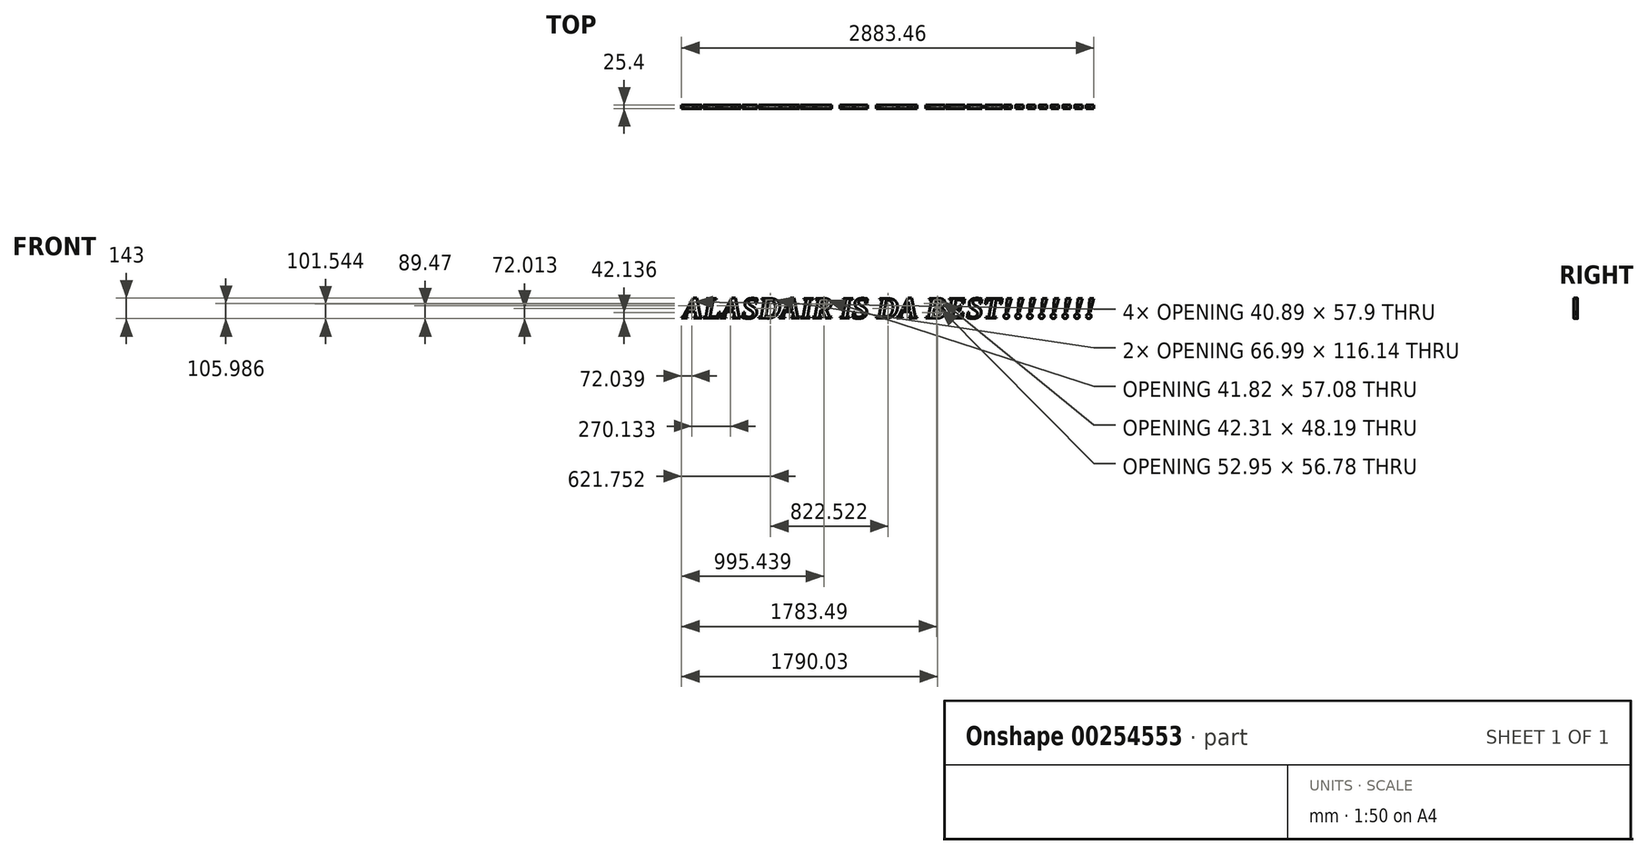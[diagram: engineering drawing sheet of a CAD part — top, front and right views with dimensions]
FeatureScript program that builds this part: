
annotation { "Feature Type Name" : "Feature", "Feature Type Description" : "" }
export const myFeature = defineFeature(function(context is Context, id is Id, definition is map)
    precondition{}
    {
        {
            var Q0;
            Q0=qCreatedBy(makeId("Front.planeOp"),FACE);
            var sketch = newSketch(context, id + "F0", { "sketchPlane" : qUnion([Q0])});
            skText(sketch, "E0", { "text": "ALASDAIR IS DA BEST!!!!!!!!", "fontName": "Tinos-BoldItalic.ttf"});
            const initialGuessF0  = {"E0": [-0.07596, -0.07625, 1, 0, 0.15221]};
            skSetInitialGuess(sketch, initialGuessF0);
            skSolve(sketch);
        }
        {
            var Q0;
            Q0 = qSketchRegion(id + "F0", true);
            var Q1;
            Q1=makeQuery(id+"F0.imprint","IMPRINT",FACE,{"disambiguationData":[TD([[makeQuery(id+"F0.imprint","IMPRINT",EDGE,{"derivedFrom":sQuery(id+"F0.wireOp",EDGE,"E0.sketch_text.stroke-382")}),-1.0]])]});
            extrude(context, id + "F1", {"entities" : qUnion([Q0, Q1]), "depth" : 25.4 * mm});
        }
    });
